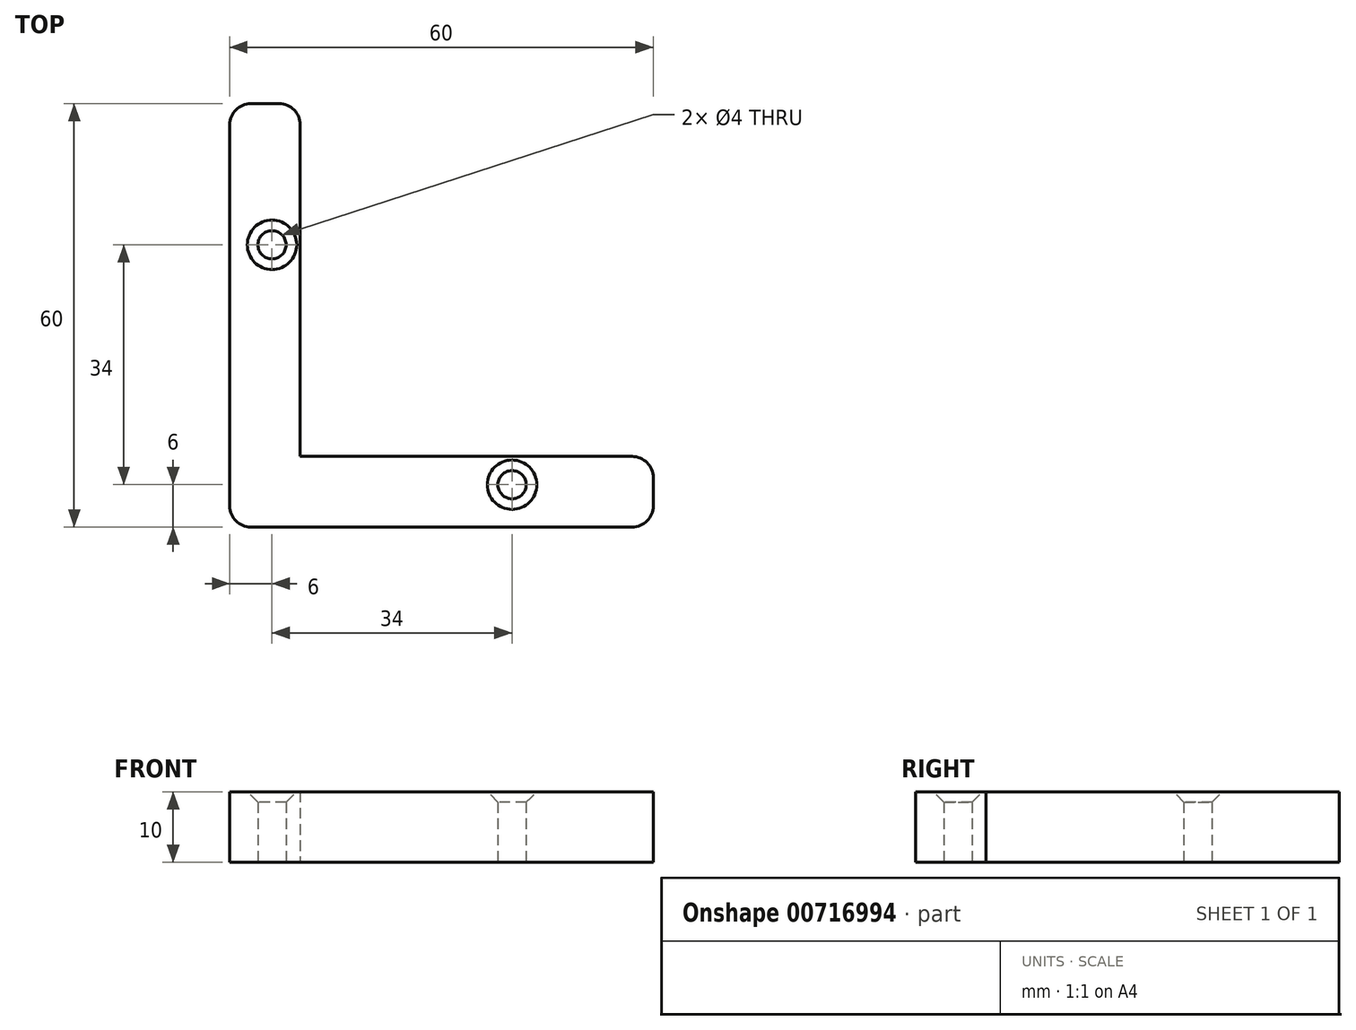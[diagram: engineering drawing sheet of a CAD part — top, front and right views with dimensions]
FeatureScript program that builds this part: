
annotation { "Feature Type Name" : "Feature", "Feature Type Description" : "" }
export const myFeature = defineFeature(function(context is Context, id is Id, definition is map)
    precondition{}
    {
        {
            var Q0;
            Q0=qCreatedBy(makeId("Top.planeOp"),FACE);
            var sketch = newSketch(context, id + "F0", { "sketchPlane" : qUnion([Q0])});
            skLineSegment(sketch, "E0", {"start": v(0, 0) * mm, "end": v(60, 0) * mm});
            skLineSegment(sketch, "E1", {"start": v(60, 0) * mm, "end": v(60, 10) * mm});
            skLineSegment(sketch, "E2", {"start": v(60, 10) * mm, "end": v(10, 10) * mm});
            skLineSegment(sketch, "E3", {"start": v(10, 10) * mm, "end": v(10, 60) * mm});
            skLineSegment(sketch, "E4", {"start": v(10, 60) * mm, "end": v(0, 60) * mm});
            skLineSegment(sketch, "E5", {"start": v(0, 60) * mm, "end": v(0, 0) * mm});
            skCircle(sketch, "E6", {"center": v(40, 6) * mm, "radius": 2 * mm});
            skLineSegment(sketch, "E7", {"start": v(0, 0) * mm, "end": v(10, 10) * mm, "construction": true});
            skCircle(sketch, "E8.MirrorC", {"center": v(6, 40) * mm, "radius": 2 * mm});
            skSolve(sketch);
        }
        {
            var Q0;
            Q0=makeQuery(id+"F0.imprint","IMPRINT",FACE,{"disambiguationData":[TD([[makeQuery(id+"F0.imprint","IMPRINT",EDGE,{"derivedFrom":sQuery(id+"F0.wireOp",EDGE,"E0")}),1.0]])]});
            extrude(context, id + "F1", {"entities" : qUnion([Q0]), "depth" : 10 * mm, "offsetDistance" : 25 * mm});
        }
        {
            var Q0;
            Q0=makeQuery(id+"F1.opExtrude","SWEPT_EDGE",EDGE,{"disambiguationData":[OSD([sQuery(id+"F0.wireOp",EDGE,"E0"),sQuery(id+"F0.wireOp",EDGE,"E5")])]});
            var Q1;
            Q1=makeQuery(id+"F1.opExtrude","SWEPT_EDGE",EDGE,{"disambiguationData":[OSD([sQuery(id+"F0.wireOp",EDGE,"E0"),sQuery(id+"F0.wireOp",EDGE,"E1")])]});
            var Q2;
            Q2=makeQuery(id+"F1.opExtrude","SWEPT_EDGE",EDGE,{"disambiguationData":[OSD([sQuery(id+"F0.wireOp",EDGE,"E1"),sQuery(id+"F0.wireOp",EDGE,"E2")])]});
            var Q3;
            Q3=makeQuery(id+"F1.opExtrude","SWEPT_EDGE",EDGE,{"disambiguationData":[OSD([sQuery(id+"F0.wireOp",EDGE,"E3"),sQuery(id+"F0.wireOp",EDGE,"E4")])]});
            var Q4;
            Q4=makeQuery(id+"F1.opExtrude","SWEPT_EDGE",EDGE,{"disambiguationData":[OSD([sQuery(id+"F0.wireOp",EDGE,"E4"),sQuery(id+"F0.wireOp",EDGE,"E5")])]});
            fillet(context, id + "F2", {"entities" : qUnion([Q0, Q1, Q2, Q3, Q4]), "radius" : 3 * mm, "tangentPropagation" : true, "allowEdgeOverflow" : false});
        }
        {
            var Q0;
            Q0=makeQuery(id+"F1.opExtrude","CAP_EDGE",EDGE,{"disambiguationData":[OSD([sQuery(id+"F0.wireOp",EDGE,"E8.MirrorC")])],"isStart":false});
            var Q1;
            Q1=makeQuery(id+"F1.opExtrude","CAP_EDGE",EDGE,{"disambiguationData":[OSD([sQuery(id+"F0.wireOp",EDGE,"E6")])],"isStart":false});
            chamfer(context, id + "F3", {"entities" : qUnion([Q0, Q1]), "width" : 1.5 * mm, "tangentPropagation" : true});
        }
    });
